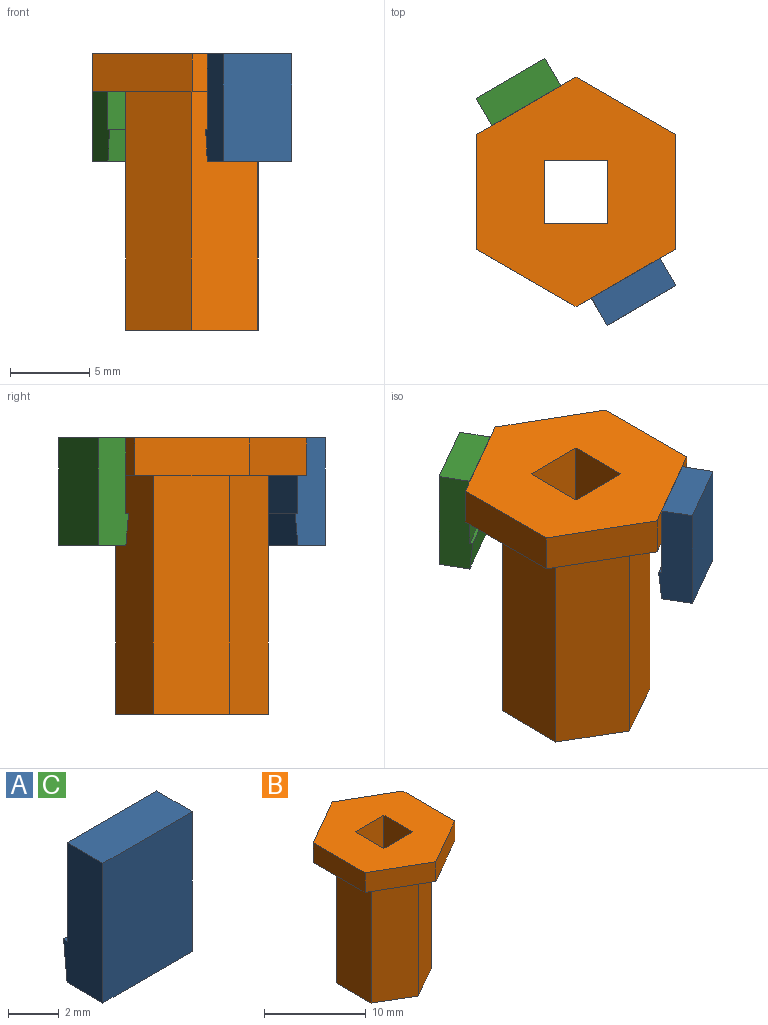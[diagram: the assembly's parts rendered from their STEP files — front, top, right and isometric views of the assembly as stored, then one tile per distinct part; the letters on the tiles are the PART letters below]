
ASSEMBLY  parts=3 mates=2
PART A: 8 faces, bbox 5x2.2x6.8 mm
  f0: plane 5x2mm, normal (0,0,1), area 10mm2, adj f1,f3,f4,f5
  f1: plane 6.76x2.2mm, normal (-1,0,0), area 13.7mm2, adj f0,f2,f4,f5,f6,f7
  f2: plane 5x2mm, normal (0,0,-1), area 10mm2, adj f1,f3,f4,f7
  f3: plane 6.76x2.2mm, normal (1,0,0), area 13.7mm2, adj f0,f2,f4,f5,f6,f7
  f4: plane 6.76x5mm, normal (0,-1,0), area 33.8mm2, adj f0,f1,f2,f3
  f5: plane 5x4.76mm, normal (0,1,0), area 23.8mm2, adj f0,f1,f3,f6
  f6: plane 5x0.2mm, normal (0,0,1), area 1mm2, adj f1,f3,f5,f7
  f7: plane 5x2mm, normal (0,1,-0.1), area 10mm2, adj f1,f2,f3,f6
PART B: 19 faces, bbox 12.5x14.4x17.4 mm
  f0: plane 15x4.8mm, normal (1,-0.01,0), area 72mm2, adj f1,f5,f6,f14
  f1: plane 15x4.14mm, normal (0.51,0.86,0), area 72mm2, adj f0,f2,f6,f14
  f2: plane 15x4.18mm, normal (-0.49,0.87,0), area 72mm2, adj f1,f3,f6,f14
  f3: plane 15x4.8mm, normal (-1,0.01,0), area 72mm2, adj f2,f4,f6,f14
  f4: plane 15x4.14mm, normal (-0.51,-0.86,0), area 72mm2, adj f3,f5,f6,f14
  f5: plane 15x4.18mm, normal (0.49,-0.87,0), area 72mm2, adj f0,f4,f6,f14
  f6: plane 9.6x8.35mm, normal (0,0,-1), area 43.9mm2, adj f0,f1,f2,f3,f4,f5,f15,f16
  f7: plane 6.25x3.61mm, normal (-0.5,0.87,0), area 17.2mm2, adj f8,f12,f13,f14
  f8: plane 7.22x2.38mm, normal (-1,0,0), area 17.2mm2, adj f7,f9,f13,f14
  f9: plane 6.25x3.61mm, normal (-0.5,-0.87,0), area 17.2mm2, adj f8,f10,f13,f14
  f10: plane 6.25x3.61mm, normal (0.5,-0.87,0), area 17.2mm2, adj f9,f11,f13,f14
  f11: plane 7.22x2.38mm, normal (1,0,0), area 17.2mm2, adj f10,f12,f13,f14
  f12: plane 6.25x3.61mm, normal (0.5,0.87,0), area 17.2mm2, adj f7,f11,f13,f14
  f13: plane 14.43x12.5mm, normal (0,0,1), area 119.3mm2, adj f7,f8,f9,f10,f11,f12,f15,f16
  f14: plane 14.43x12.5mm, normal (0,0,-1), area 75.5mm2, adj f0,f1,f2,f3,f4,f5,f7,f8
  f15: plane 17.38x4mm, normal (1,0,0), area 69.5mm2, adj f6,f13,f16,f18
  f16: plane 17.38x4mm, normal (0,1,0), area 69.5mm2, adj f6,f13,f15,f17
  f17: plane 17.38x4mm, normal (-1,0,0), area 69.5mm2, adj f6,f13,f16,f18
  f18: plane 17.38x4mm, normal (0,-1,0), area 69.5mm2, adj f6,f13,f15,f17
PART C: same geometry as A
PLACE A rot(axis=(0,0,1),30deg) t=(-4.47,6.83,8.21)mm
PLACE B t=(-3.18,2.61,-1.77)mm
PLACE C rot(axis=(0,0,-1),150deg) t=(-1.88,22.76,8.21)mm
MATE fastened C.f5 <-> B.f7  axis (0.5,-0.87,0) through (-6.3,20.2,15.61)mm
MATE fastened A.f5 <-> B.f10  axis (-0.5,0.87,0) through (-0.05,9.38,15.61)mm
